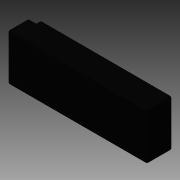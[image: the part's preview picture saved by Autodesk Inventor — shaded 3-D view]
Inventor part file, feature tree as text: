
AUTODESK INVENTOR PART (.ipt)
format: ipt  version: 2015 (Build 190159000, 159)  size: 203,776 bytes
history: native  units: mm
features: extrude x4, fillet x4, sketch x2
ambient origin geometry x8: Origin, YZ Plane, XZ Plane, XY Plane, X Axis, Y Axis, Z Axis, Center Point
bodies: Solid1 (feature_tree)
feature tree (10):
  sketch  "Sketch1"  dims[d0=138.42mm d1=46.73mm]
  extrude  "Extrusion1"  Depth=46.73mm
  extrude  "Extrusion2"  Depth=0.25mm
  extrude  "Extrusion3"  Depth=0.25mm
  extrude  "Extrusion4"  Depth=0.25mm
  fillet  "Fillet1"  Radius=4.525mm
  fillet  "Fillet2"  Radius=4.525mm
  fillet  "Fillet3"  Radius=8.365mm
  fillet  "Fillet4"  Radius=8.365mm
  sketch  "Sketch3"  dims[d2=4.0mm d3=4.0mm d5=4.525mm d7=4.525mm d11=4.525mm d13=4.525mm d14=8.365mm d15=8.365mm d16=2.0mm d17=2.0mm d18=25.3mm d19=0.0mm d20=20.2mm d21=0.0mm d22=6.0mm d23=0.0mm d24=11.1mm d25=0.0mm d26=2.0mm d27=1.0mm d28=0.25mm d29=0.25mm d34=18.84mm]
